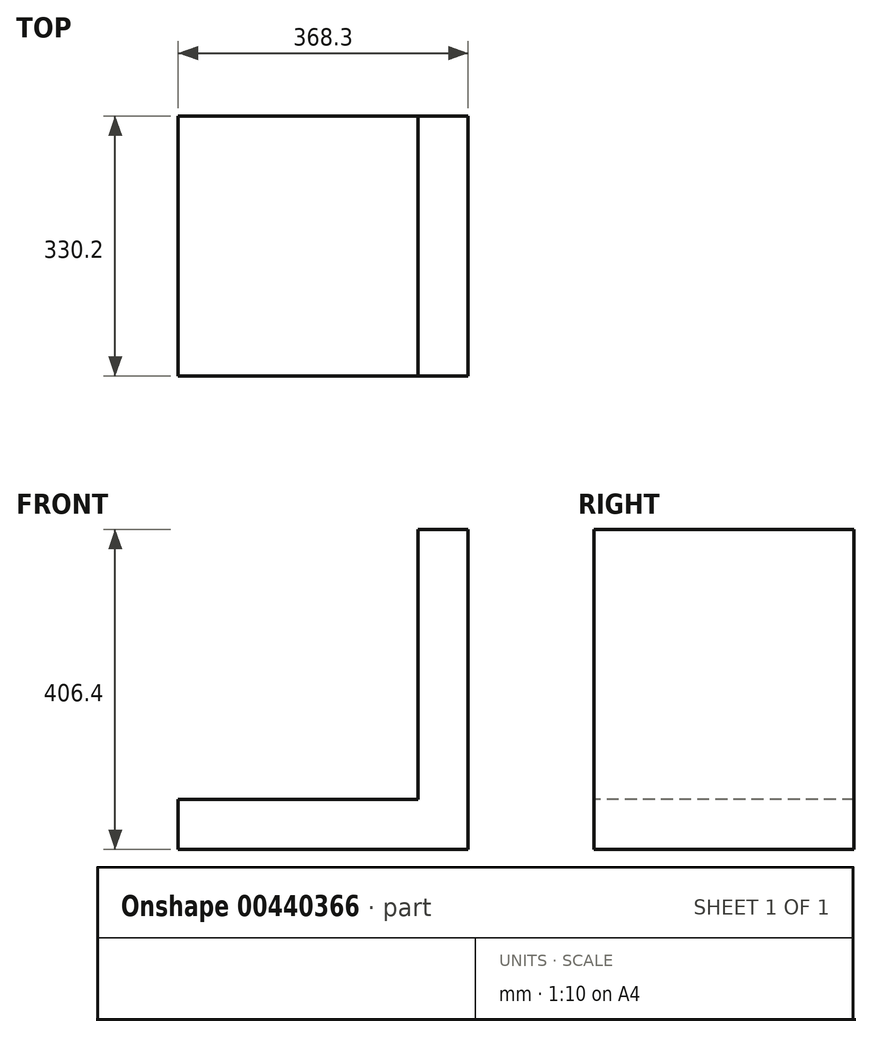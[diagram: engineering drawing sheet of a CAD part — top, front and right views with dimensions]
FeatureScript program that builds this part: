
annotation { "Feature Type Name" : "Feature", "Feature Type Description" : "" }
export const myFeature = defineFeature(function(context is Context, id is Id, definition is map)
    precondition{}
    {
        {
            var Q0;
            Q0=qCreatedBy(makeId("Front.planeOp"),FACE);
            var sketch = newSketch(context, id + "F0", { "sketchPlane" : qUnion([Q0])});
            skLineSegment(sketch, "E0.bottom", {"start": v(0, 0) * mm, "end": v(-304.8, 0) * mm});
            skLineSegment(sketch, "E0.top", {"start": v(0, -63.5) * mm, "end": v(-304.8, -63.5) * mm});
            skLineSegment(sketch, "E0.left", {"start": v(0, 0) * mm, "end": v(0, -63.5) * mm});
            skLineSegment(sketch, "E0.right", {"start": v(-304.8, 0) * mm, "end": v(-304.8, -63.5) * mm});
            skLineSegment(sketch, "E1.bottom", {"start": v(0, -63.5) * mm, "end": v(63.5, -63.5) * mm});
            skLineSegment(sketch, "E1.top", {"start": v(0, 342.9) * mm, "end": v(63.5, 342.9) * mm});
            skLineSegment(sketch, "E1.left", {"start": v(0, -63.5) * mm, "end": v(0, 342.9) * mm});
            skLineSegment(sketch, "E1.right", {"start": v(63.5, -63.5) * mm, "end": v(63.5, 342.9) * mm});
            skSolve(sketch);
        }
        {
            var Q0;
            {var subQ3=sQuery(id+"F0.wireOp",EDGE,"E1.bottom");Q0=makeQuery(id+"F0.imprint","IMPRINT",FACE,{"disambiguationData":[TD([[makeQuery(id+"F0.imprint","IMPRINT",EDGE,{"derivedFrom":subQ3}),1.0]])]});}
            extrude(context, id + "F1", {"entities" : qUnion([Q0]), "endBound" : BoundingType.SYMMETRIC, "depth" : 330.2 * mm});
        }
        {
            var Q0;
            Q0=makeQuery(id+"F1.opExtrude","CAP_FACE",FACE,{"disambiguationData":[OSD([sQuery(id+"F0.wireOp",EDGE,"E1.bottom"),sQuery(id+"F0.wireOp",EDGE,"E1.top"),sQuery(id+"F0.wireOp",EDGE,"E1.left"),sQuery(id+"F0.wireOp",EDGE,"E1.right")])],"isStart":false});
            var sketch = newSketch(context, id + "F2", { "sketchPlane" : qUnion([Q0])});
            skLineSegment(sketch, "E2.bottom", {"start": v(0, 0) * mm, "end": v(-304.8, 0) * mm});
            skLineSegment(sketch, "E2.top", {"start": v(0, -63.5) * mm, "end": v(-304.8, -63.5) * mm});
            skLineSegment(sketch, "E2.left", {"start": v(0, 0) * mm, "end": v(0, -63.5) * mm});
            skLineSegment(sketch, "E2.right", {"start": v(-304.8, 0) * mm, "end": v(-304.8, -63.5) * mm});
            skSolve(sketch);
        }
        {
            var Q0;
            Q0=makeQuery(id+"F2.imprint","IMPRINT",FACE,{"disambiguationData":[TD([[makeQuery(id+"F2.imprint","IMPRINT",EDGE,{"derivedFrom":sQuery(id+"F2.wireOp",EDGE,"E2.bottom")}),1.0]])]});
            extrude(context, id + "F3", {"entities" : qUnion([Q0]), "operationType" : NewBodyOperationType.ADD, "depth" : -330.2 * mm});
        }
    });
